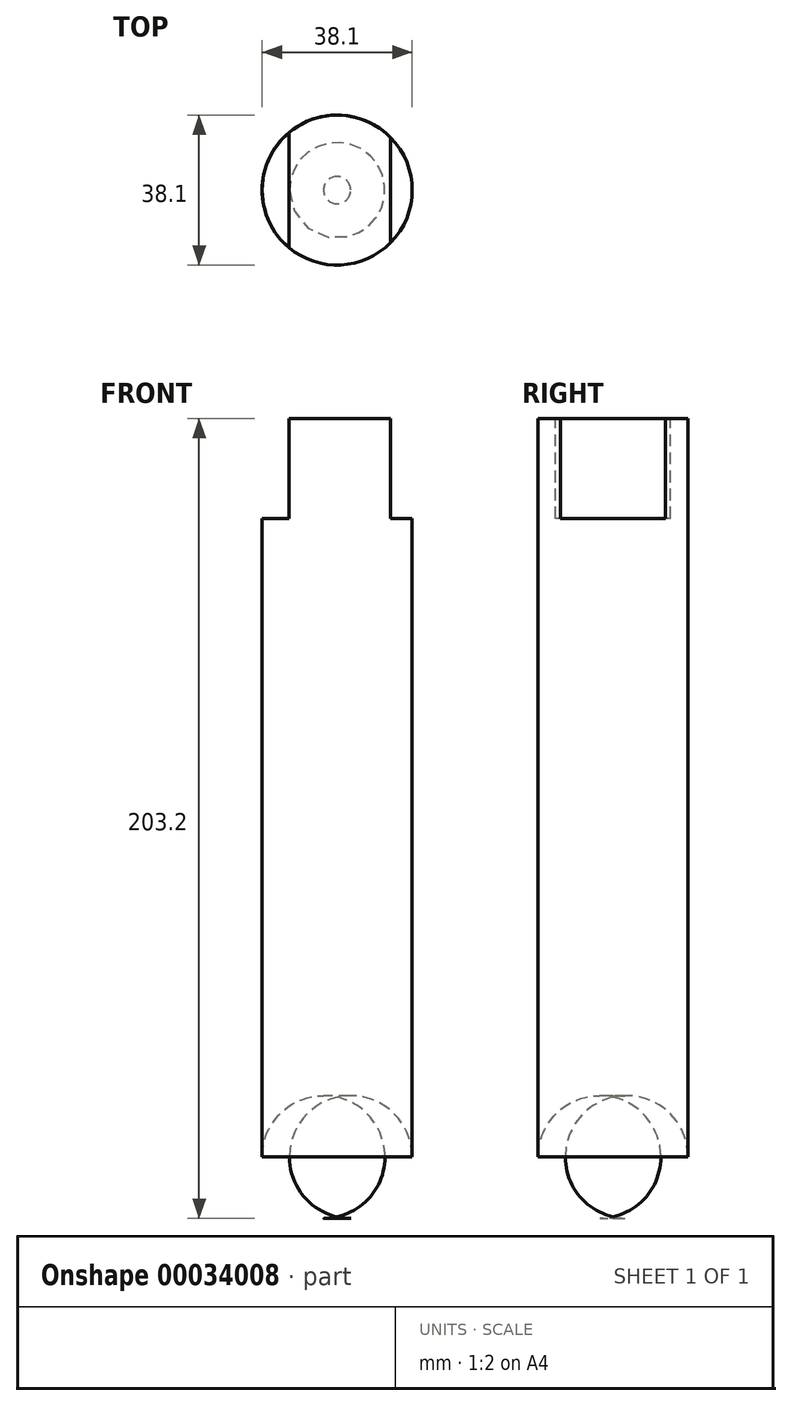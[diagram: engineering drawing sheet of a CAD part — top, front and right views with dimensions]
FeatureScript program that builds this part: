
annotation { "Feature Type Name" : "Feature", "Feature Type Description" : "" }
export const myFeature = defineFeature(function(context is Context, id is Id, definition is map)
    precondition{}
    {
        {
            var Q0;
            Q0=qCreatedBy(makeId("Top.planeOp"),FACE);
            var sketch = newSketch(context, id + "F0", { "sketchPlane" : qUnion([Q0])});
            skCircle(sketch, "E0", {"center": v(0, 0) * mm, "radius": 19.05 * mm});
            skSolve(sketch);
        }
        {
            var Q0;
            Q0 = qSketchRegion(id + "F0", true);
            extrude(context, id + "F1", {"entities" : qUnion([Q0]), "depth" : 203.2 * mm});
        }
        {
            var Q0;
            Q0=makeQuery(id+"F1.opExtrude","CAP_FACE",FACE,{"disambiguationData":[OSD([sQuery(id+"F0.wireOp",EDGE,"E0")])],"isStart":false});
            var sketch = newSketch(context, id + "F2", { "sketchPlane" : qUnion([Q0])});
            skCircle(sketch, "E1.0", {"center": v(0, 0) * mm, "radius": 19.05 * mm});
            skLineSegment(sketch, "E2.bottom", {"start": v(-12.24, 24.88) * mm, "end": v(13.61, 24.88) * mm});
            skLineSegment(sketch, "E2.top", {"start": v(-12.24, -34.47) * mm, "end": v(13.61, -34.47) * mm});
            skLineSegment(sketch, "E2.left", {"start": v(-12.24, 24.88) * mm, "end": v(-12.24, -34.47) * mm});
            skLineSegment(sketch, "E2.right", {"start": v(13.61, 24.88) * mm, "end": v(13.61, -34.47) * mm});
            skSolve(sketch);
        }
        {
            var Q0;
            {var subQ0=sQuery(id+"F2.wireOp",EDGE,"E2.left");var subQ1=sQuery(id+"F2.wireOp",EDGE,"E1.0");var subQ3=makeQuery(id+"F2.imprint","INTERSECT",VERTEX,{"disambiguationData":[OD(0.0)],"derivedFrom":[subQ1,subQ0]});Q0=makeQuery(id+"F2.imprint","IMPRINT",FACE,{"disambiguationData":[TD([[makeQuery(id+"F2.imprint","IMPRINT",EDGE,{"disambiguationData":[TD([[subQ3,-1.0]])],"derivedFrom":subQ1}),1.0]])]});}
            extrude(context, id + "F3", {"entities" : qUnion([Q0]), "operationType" : NewBodyOperationType.REMOVE, "oppositeDirection" : true, "depth" : 25.4 * mm});
        }
        {
            var Q0;
            {var subQ0=sQuery(id+"F2.wireOp",EDGE,"E2.right");var subQ1=sQuery(id+"F2.wireOp",EDGE,"E1.0");var subQ3=makeQuery(id+"F2.imprint","INTERSECT",VERTEX,{"disambiguationData":[OD(0.0)],"derivedFrom":[subQ1,subQ0]});Q0=makeQuery(id+"F2.imprint","IMPRINT",FACE,{"disambiguationData":[TD([[makeQuery(id+"F2.imprint","IMPRINT",EDGE,{"disambiguationData":[TD([[subQ3,1.0]])],"derivedFrom":subQ1}),1.0]])]});}
            extrude(context, id + "F4", {"entities" : qUnion([Q0]), "operationType" : NewBodyOperationType.REMOVE, "oppositeDirection" : true, "depth" : 25.4 * mm});
        }
        {
            var Q0;
            Q0=makeQuery(id+"F1.opExtrude","CAP_EDGE",EDGE,{"disambiguationData":[OSD([sQuery(id+"F0.wireOp",EDGE,"E0")])],"isStart":true});
            fillet(context, id + "F5", {"entities" : qUnion([Q0]), "radius" : 15.6 * mm, "tangentPropagation" : true, "allowEdgeOverflow" : false});
        }
    });
